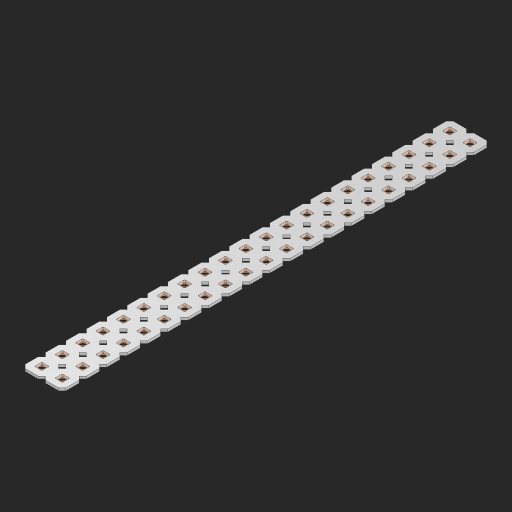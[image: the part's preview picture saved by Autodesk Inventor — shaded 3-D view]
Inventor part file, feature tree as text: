
AUTODESK INVENTOR PART (.ipt)
format: ipt  version: 2023 (Build 270158000, 158)  size: 755,200 bytes
history: native  units: in
note: dims shown in document units (in); Inventor stores cm internally (conversion verified against a paired STEP export)
features: other x43, extrude x41, sketch x2, pattern_linear x1
ambient origin geometry x8: Origin, YZ Plane, XZ Plane, XY Plane, X Axis, Y Axis, Z Axis, Center Point
bodies: Solid1 (feature_tree), Body (feature_tree)
feature tree (87):
  pattern_linear  "Rectangular Pattern1"  Spacing1=0.09in  [1 undecoded]
  sketch  "Sketch1"  dims[d1=0.5in]
  sketch  "Sketch2"  dims[d2=0.182in d3=0.09in d4=0.09in d5=0.09in d6=0.09in d7=0.09in d8=0.09in d9=0.09in d10=0.09in d11=0.02in d13=0.0in d14=0.172in d15=0.0625in d16=0.0in d19=0.5in d22=0.5in]
  other  "Srf1"
  other  "Srf126"
  other  "Srf127"
  other  "Srf128"
  other  "Srf129"
  other  "Srf130"
  other  "Srf131"
  other  "Srf250"
  other  "Srf251"
  other  "Srf252"
  other  "Srf253"
  other  "Srf254"
  other  "Srf255"
  other  "Srf256"
  other  "Srf257"
  other  "Srf258"
  other  "Srf259"
  other  "Srf260"
  other  "Srf261"
  other  "Srf262"
  other  "Srf263"
  other  "Srf268"
  other  "Srf269"
  other  "Srf270"
  other  "Srf271"
  other  "Srf272"
  other  "Srf273"
  other  "Srf274"
  other  "Srf275"
  other  "Srf276"
  other  "Srf277"
  other  "Srf278"
  other  "Srf279"
  other  "Srf280"
  other  "Srf281"
  other  "Srf282"
  other  "Srf283"
  other  "Srf284"
  other  "Srf285"
  other  "Srf286"
  other  "Srf287"
  other  "Srf288"
  other  "Circle"
  extrude  "ExtrusionSrf126"  Depth=0.09in
  extrude  "ExtrusionSrf127"  Depth=0.09in
  extrude  "ExtrusionSrf128"  Depth=0.09in
  extrude  "ExtrusionSrf129"  Depth=0.09in
  extrude  "ExtrusionSrf130"  Depth=0.09in
  extrude  "ExtrusionSrf131"  Depth=0.09in
  extrude  "ExtrusionSrf250"  Depth=0.09in
  extrude  "ExtrusionSrf251"  Depth=0.02in
  extrude  "ExtrusionSrf252"  TaperAngle=0.0deg  [1 undecoded]
  extrude  "ExtrusionSrf253"  Depth=0.5in
  extrude  "ExtrusionSrf254"  Depth=0.0625in TaperAngle=0.0deg
  extrude  "ExtrusionSrf255"  Depth=0.5in
  extrude  "ExtrusionSrf256"  Depth=0.5in
  extrude  "ExtrusionSrf257"  [1 undecoded]
  extrude  "ExtrusionSrf258"  [1 undecoded]
  extrude  "ExtrusionSrf259"  [1 undecoded]
  extrude  "ExtrusionSrf260"  [1 undecoded]
  extrude  "ExtrusionSrf261"  [1 undecoded]
  extrude  "ExtrusionSrf262"  [1 undecoded]
  extrude  "ExtrusionSrf263"  [1 undecoded]
  extrude  "ExtrusionSrf268"  [1 undecoded]
  extrude  "ExtrusionSrf269"  [1 undecoded]
  extrude  "ExtrusionSrf270"  [1 undecoded]
  extrude  "ExtrusionSrf271"  [1 undecoded]
  extrude  "ExtrusionSrf272"  [1 undecoded]
  extrude  "ExtrusionSrf273"  [1 undecoded]
  extrude  "ExtrusionSrf274"  [1 undecoded]
  extrude  "ExtrusionSrf275"  [1 undecoded]
  extrude  "ExtrusionSrf276"  [1 undecoded]
  extrude  "ExtrusionSrf277"  [1 undecoded]
  extrude  "ExtrusionSrf278"  [1 undecoded]
  extrude  "ExtrusionSrf279"  [1 undecoded]
  extrude  "ExtrusionSrf280"  [1 undecoded]
  extrude  "ExtrusionSrf281"  [1 undecoded]
  extrude  "ExtrusionSrf282"  [1 undecoded]
  extrude  "ExtrusionSrf283"  [1 undecoded]
  extrude  "ExtrusionSrf284"  [1 undecoded]
  extrude  "ExtrusionSrf285"  [1 undecoded]
  extrude  "ExtrusionSrf286"  [1 undecoded]
  extrude  "ExtrusionSrf287"  [1 undecoded]
  extrude  "ExtrusionSrf288"  [1 undecoded]
note: 30 required parameter values undecoded (feature->parameter linkage not recoverable at this tier; creation-order binding heuristic only, values carry confidence <= 0.55)
